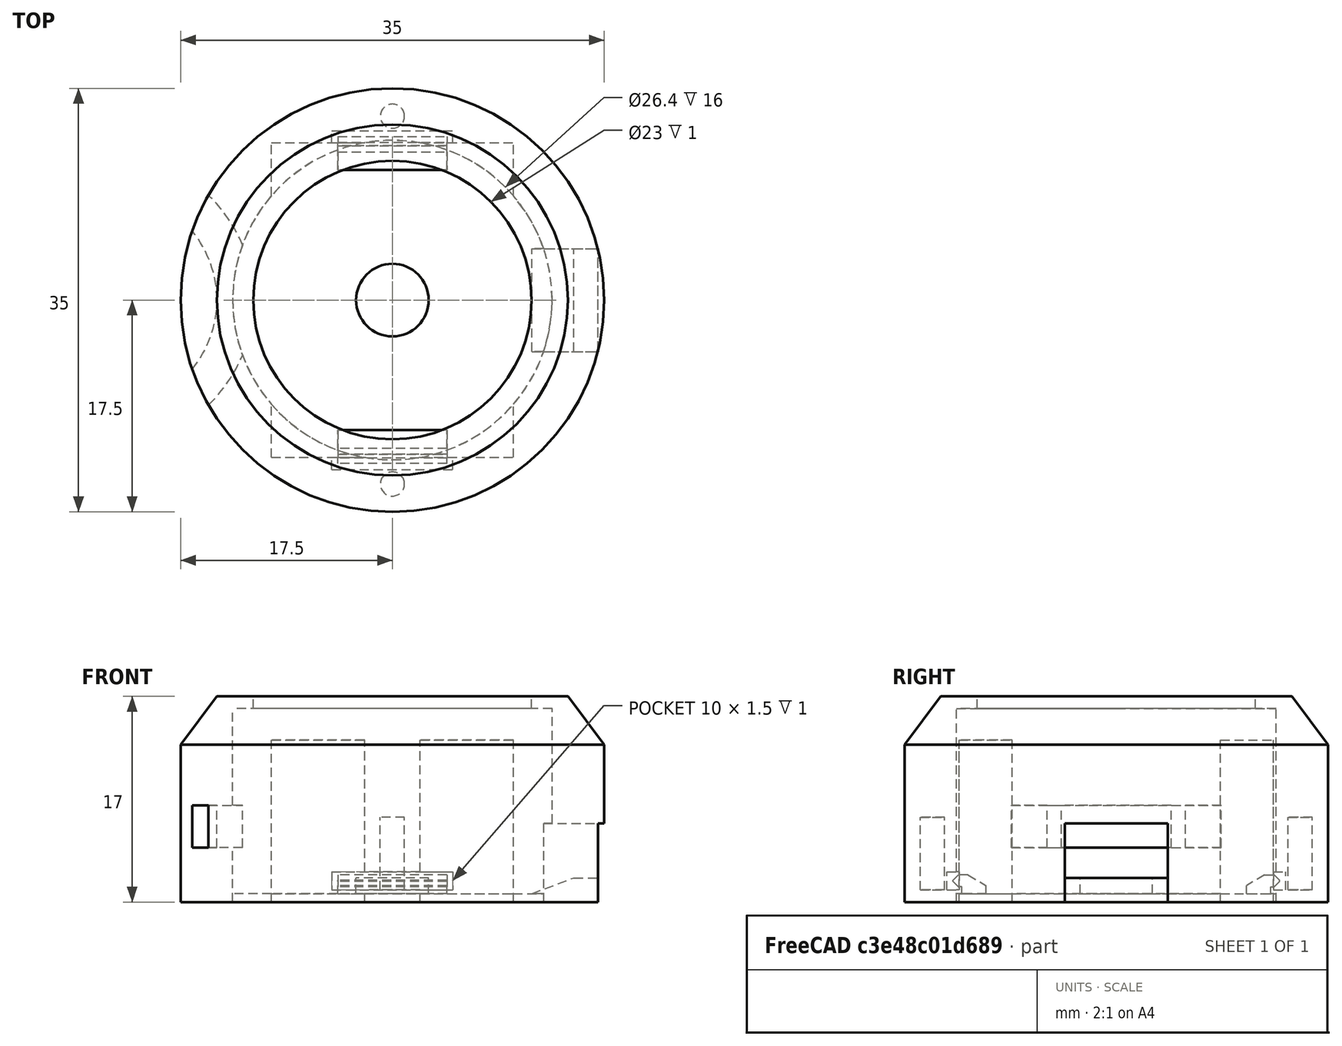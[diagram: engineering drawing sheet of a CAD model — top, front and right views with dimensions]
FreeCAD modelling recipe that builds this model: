
FCSTD DOCUMENT  (FreeCAD 0.15R4630 (Git))
Label: Pendant
License: All rights reserved
LicenseURL: http://en.wikipedia.org/wiki/All_rights_reserved
objects: Part::Cylinder×9, Part::Box×8, Part::Chamfer×5, Part::MultiFuse×3, Part::Cut×2
note: 27 computed .brp shape members not serialized (recipe doc carries the construction recipe); baked Part::Feature solids carry a one-line shape summary decoded from their .brp

FEATURE [Part::Cylinder] Cylinder002  label="DiffuserHole"
  Angle = 360
  Height = 30
  Radius = 11.5
FEATURE [Part::Cylinder] Cylinder  label="PCB Hole"
  Angle = 360
  Height = 16
  Placement = pos=(0,0,-1) rot=(0,0,1;0rad)
  Radius = 13.2
FEATURE [Part::Cylinder] Cylinder006  label="MainBody"
  Angle = 360
  Height = 17
  Placement = pos=(0,0,-1) rot=(0,0,1;0rad)
  Radius = 17.5
FEATURE [Part::Box] Box  label="BatteryHole"
  Height = 13.4
  Length = 20
  Placement = pos=(-10,-13,-1) rot=(0,0,1;0rad)
  Width = 26
FEATURE [Part::Box] Box001  label="USB"
  Height = 7
  Length = 16
  Placement = pos=(7,-4.25,-1.5) rot=(0,0,1;0rad)
  Width = 8.5
FEATURE [Part::Cylinder] Cylinder007  label="R Screw"
  Angle = 360
  Height = 6
  Placement = pos=(0,-15.2,0) rot=(0,0,1;0rad)
  Radius = 1
FEATURE [Part::Cylinder] Cylinder008  label="L Screw"
  Angle = 360
  Height = 6
  Placement = pos=(0,15.2,0) rot=(0,0,1;0rad)
  Radius = 1
FEATURE [Part::Chamfer] Chamfer  label="MainBody Chamfered"
  Base = -> Cylinder006
  Edges = 1 edges: [Edge1 r1=4 r2=3]
FEATURE [Part::Cylinder] Cylinder016  label="Button Presser"
  Angle = 360
  Height = 1.5
  Placement = pos=(0,0,-0.5) rot=(0,0,1;0rad)
  Radius = 3
FEATURE [Part::Cylinder] Cylinder017  label="Cylinder"
  Angle = 360
  Height = 3.5
  Placement = pos=(-23.5,0,3.5) rot=(0,0,1;0rad)
  Radius = 12
FEATURE [Part::Cylinder] Cylinder018  label="Cylinder001"
  Angle = 360
  Height = 3.5
  Placement = pos=(-23.5,0,3.5) rot=(0,0,1;0rad)
  Radius = 9
FEATURE [Part::Cut] Cut002  label="Chain Channel"
  Base = -> Cylinder017
  Tool = -> Cylinder018
FEATURE [Part::Box] Box002  label="BatteryHole001"
  Height = 0.7
  Length = 20
  Placement = pos=(-10,-13,-1) rot=(0,0,1;0rad)
  Width = 26
FEATURE [Part::Cylinder] Cylinder019  label="PCB Hole001"
  Angle = 360
  Height = 0.7
  Placement = pos=(0,0,-1) rot=(0,0,1;0rad)
  Radius = 13.2
FEATURE [Part::Box] Box003  label="USB Cover Base"
  Height = 2
  Length = 6
  Placement = pos=(11,-4.25,-1) rot=(0,0,1;0rad)
  Width = 8.5
FEATURE [Part::Box] Box004  label="Tab"
  Height = 1
  Length = 9
  Placement = pos=(-4.5,10.75,0.25) rot=(0,0,1;0rad)
  Width = 2.75
FEATURE [Part::Box] Box006  label="Tab 2 Female"
  Height = 1.5
  Length = 10
  Placement = pos=(-5,-14,0) rot=(0,0,1;0rad)
  Width = 2
FEATURE [Part::Box] Box007  label="Tab 1 Female"
  Height = 1.5
  Length = 10
  Placement = pos=(-5,12,0) rot=(0,0,1;0rad)
  Width = 2
FEATURE [Part::MultiFuse] Fusion  label="Guts"
  Shapes = -> [Cylinder,Cylinder002,Box,Box001,Cut002,Box006,Box007]
FEATURE [Part::Cut] Cut  label="Front"
  Base = -> Chamfer
  Tool = -> Fusion
FEATURE [Part::Chamfer] Chamfer004  label="USB Cover"
  Base = -> Box003
  Edges = 1 edges: [Edge2 r1=1.5 r2=4]
FEATURE [Part::Box] Box008  label="Tab Base"
  Height = 1
  Length = 9
  Placement = pos=(-4.5,10.75,-0.75) rot=(0,0,1;0rad)
  Width = 2
FEATURE [Part::MultiFuse] Fusion002
  Shapes = -> [Box004,Box008]
FEATURE [Part::Chamfer] Chamfer005
  Base = -> Fusion002
  Edges = 1 edges: [Edge4 r1=1.5 r2=0.9]
FEATURE [Part::Chamfer] Chamfer006  label="Tab 2"
  Base = -> Chamfer005
  Edges = 2 edges r=0.45: [Edge3,Edge12]
  Placement = pos=(0,0,0) rot=(0,0,1;3.14159rad)
FEATURE [Part::Chamfer] Chamfer007  label="Tab 1"
  Base = -> Chamfer005
  Edges = 2 edges r=0.45: [Edge3,Edge12]
FEATURE [Part::MultiFuse] Fusion001  label="Back"
  Shapes = -> [Cylinder019,Box002,Cylinder016,Chamfer004,Chamfer006,Chamfer007]
